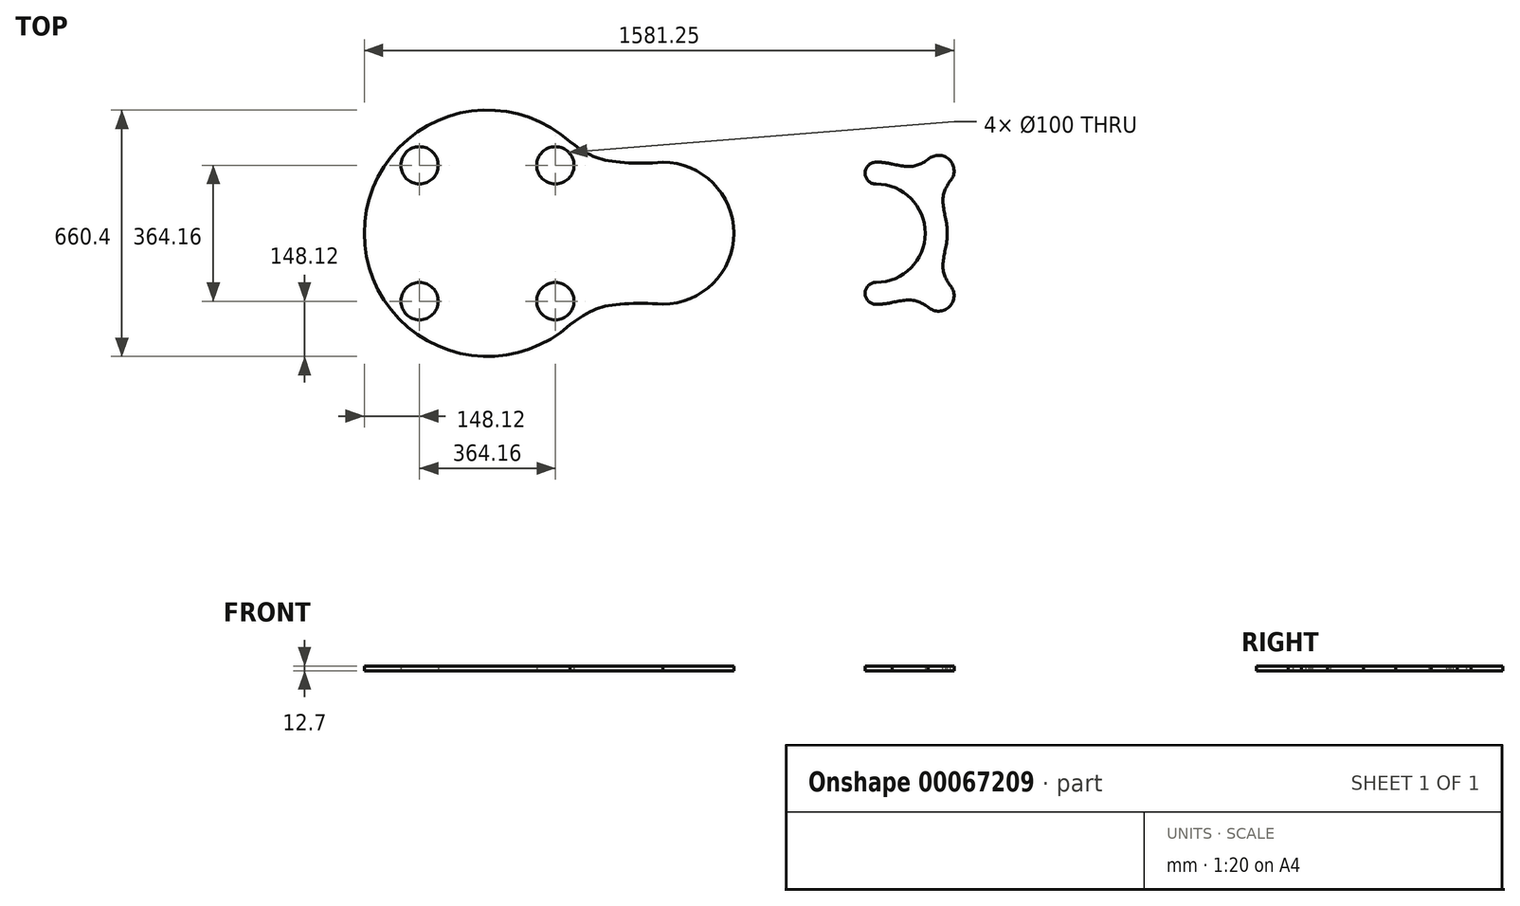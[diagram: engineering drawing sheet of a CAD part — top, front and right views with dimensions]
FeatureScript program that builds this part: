
annotation { "Feature Type Name" : "Feature", "Feature Type Description" : "" }
export const myFeature = defineFeature(function(context is Context, id is Id, definition is map)
    precondition{}
    {
        {
            var Q0;
            Q0=qCreatedBy(makeId("Top.planeOp"),FACE);
            var sketch = newSketch(context, id + "F0", { "sketchPlane" : qUnion([Q0])});
            skArc(sketch, "E0", {"start": v(221.34, 245.03) * mm, "mid": v(-330.2, 0) * mm, "end": v(221.34, -245.03) * mm});
            skLineSegment(sketch, "E1", {"start": v(1366.65, 0) * mm, "end": v(-609.6, 0) * mm, "construction": true});
            skLineSegment(sketch, "E2", {"start": v(0, -453.97) * mm, "end": v(0, 473.73) * mm, "construction": true});
            skCircle(sketch, "E3", {"center": v(182.08, 182.08) * mm, "radius": 50 * mm});
            skLineSegment(sketch, "E4", {"start": v(0, 0) * mm, "end": v(484.14, 484.14) * mm, "construction": true});
            skCircle(sketch, "E5.1.0", {"center": v(-182.08, 182.08) * mm, "radius": 50 * mm});
            skCircle(sketch, "E5.2.0", {"center": v(-182.08, -182.08) * mm, "radius": 50 * mm});
            skCircle(sketch, "E5.3.0", {"center": v(182.08, -182.08) * mm, "radius": 50 * mm});
            skArc(sketch, "E6", {"start": v(469.9, -190.5) * mm, "mid": v(660.4, 0) * mm, "end": v(469.9, 190.5) * mm});
            skLineSegment(sketch, "E7", {"start": v(469.9, -429.61) * mm, "end": v(469.9, 571.15) * mm, "construction": true});
            skFitSpline(sketch, "E8", {"points": [v(469.9, 190.5) * mm, v(322.58, 194.75) * mm, v(221.34, 245.03) * mm], "startDerivative": vector(-310.61, -30.4) * mm, "endDerivative": vector(-314.3, 226.46) * mm});
            skFitSpline(sketch, "E9.MirrorCS", {"points": [v(469.9, -190.5) * mm, v(322.58, -194.75) * mm, v(221.34, -245.03) * mm], "startDerivative": vector(-310.61, 30.4) * mm, "endDerivative": vector(-314.3, -226.46) * mm});
            skArc(sketch, "E10", {"start": v(1085.08, 185.57) * mm, "mid": v(1063.7, 189.26) * mm, "end": v(1042.04, 190.5) * mm});
            skArc(sketch, "E11", {"start": v(1173.8, 0) * mm, "mid": v(1135.2, 93.17) * mm, "end": v(1042.04, 131.76) * mm});
            skLineSegment(sketch, "E12", {"start": v(1042.04, 0) * mm, "end": v(1494.15, 452.11) * mm, "construction": true});
            skLineSegment(sketch, "E13.MirrorCS", {"start": v(1042.04, 324.62) * mm, "end": v(1042.04, -1651.64) * mm, "construction": true});
            skArc(sketch, "E14", {"start": v(1239.73, 139.34) * mm, "mid": v(1238.96, 196.92) * mm, "end": v(1181.38, 197.7) * mm});
            skFitSpline(sketch, "E15", {"points": [v(1181.38, 197.7) * mm, v(1141.38, 179.68) * mm, v(1085.08, 185.57) * mm], "startDerivative": vector(-80.35, -50.36) * mm, "endDerivative": vector(-111.4, 23.93) * mm});
            skFitSpline(sketch, "E16.MirrorCS", {"points": [v(1239.73, 139.34) * mm, v(1221.72, 99.35) * mm, v(1227.6, 43.04) * mm], "startDerivative": vector(-50.36, -80.35) * mm, "endDerivative": vector(23.93, -111.4) * mm});
            skArc(sketch, "E17.trimOffspring", {"start": v(1232.54, 0) * mm, "mid": v(1231.3, 21.66) * mm, "end": v(1227.6, 43.04) * mm});
            skFitSpline(sketch, "E18.MirrorCS", {"points": [v(1181.38, -197.7) * mm, v(1141.38, -179.68) * mm, v(1085.08, -185.57) * mm], "startDerivative": vector(-80.35, 50.36) * mm, "endDerivative": vector(-111.4, -23.93) * mm});
            skFitSpline(sketch, "E19.MirrorCS", {"points": [v(1239.73, -139.34) * mm, v(1221.72, -99.35) * mm, v(1227.6, -43.04) * mm], "startDerivative": vector(-50.36, 80.35) * mm, "endDerivative": vector(23.93, 111.4) * mm});
            skArc(sketch, "E20.MirrorCS", {"start": v(1173.8, 0) * mm, "mid": v(1135.2, -93.17) * mm, "end": v(1042.04, -131.76) * mm});
            skArc(sketch, "E21.MirrorCS", {"start": v(1232.54, 0) * mm, "mid": v(1231.3, -21.66) * mm, "end": v(1227.6, -43.04) * mm});
            skArc(sketch, "E22.MirrorCS", {"start": v(1239.73, -139.34) * mm, "mid": v(1238.96, -196.92) * mm, "end": v(1181.38, -197.7) * mm});
            skArc(sketch, "E23.MirrorCS", {"start": v(1085.08, -185.57) * mm, "mid": v(1063.7, -189.26) * mm, "end": v(1042.04, -190.5) * mm});
            skArc(sketch, "E24", {"start": v(1042.04, 190.5) * mm, "mid": v(1012.67, 161.13) * mm, "end": v(1042.04, 131.76) * mm});
            skArc(sketch, "E25.MirrorCS", {"start": v(1042.04, -190.5) * mm, "mid": v(1012.67, -161.13) * mm, "end": v(1042.04, -131.76) * mm});
            skPoint(sketch, "E26.orphan", {"position": v(851.54, 0) * mm});
            skPoint(sketch, "E27.orphan", {"position": v(910.27, 0) * mm});
            skSolve(sketch);
        }
        {
            var Q0;
            Q0=makeQuery(id+"F0.imprint","IMPRINT",FACE,{"disambiguationData":[TD([[makeQuery(id+"F0.imprint","IMPRINT",EDGE,{"derivedFrom":sQuery(id+"F0.wireOp",EDGE,"E3")}),-1.0]])]});
            var Q1;
            Q1=makeQuery(id+"F0.imprint","IMPRINT",FACE,{"disambiguationData":[TD([[makeQuery(id+"F0.imprint","IMPRINT",EDGE,{"derivedFrom":sQuery(id+"F0.wireOp",EDGE,"E10")}),1.0]])]});
            extrude(context, id + "F1", {"entities" : qUnion([Q0, Q1]), "depth" : 12.7 * mm});
        }
    });
